FCSTD DOCUMENT  (FreeCAD 1.0R39319 (Git))
Label: trofast-fix
License: All rights reserved
LicenseURL: https://en.wikipedia.org/wiki/All_rights_reserved
objects: Sketcher::SketchObject×1
note: 2 computed .brp shape members not serialized (recipe doc carries the construction recipe); baked Part::Feature solids carry a one-line shape summary decoded from their .brp

FEATURE [Sketcher::SketchObject] Sketch
  ArcFitTolerance = 1e-06
  FullyConstrained = true
  MakeInternals = false
  sketch-geometry (18):
    g0: LineSegment StartX=207.5 StartY=-7.5 StartZ=0 EndX=207.5 EndY=7.5 EndZ=0
    g1: LineSegment StartX=202.5 StartY=12.5 StartZ=0 EndX=-202.5 EndY=12.5 EndZ=0
    g2: LineSegment StartX=-207.5 StartY=7.5 StartZ=0 EndX=-207.5 EndY=-7.5 EndZ=0
    g3: LineSegment StartX=-202.5 StartY=-12.5 StartZ=0 EndX=202.5 EndY=-12.5 EndZ=0
    g4: GeomPoint [constr] X=0 Y=0 Z=0
    g5: Circle CenterX=-182.5 CenterY=0 CenterZ=0 NormalX=0 NormalY=0 NormalZ=1 AngleXU=0 Radius=2
    g6: Circle CenterX=0 CenterY=0 CenterZ=0 NormalX=0 NormalY=0 NormalZ=1 AngleXU=0 Radius=2
    g7: Circle CenterX=182.5 CenterY=0 CenterZ=0 NormalX=0 NormalY=0 NormalZ=1 AngleXU=0 Radius=2
    g8: LineSegment [constr] StartX=-182.5 StartY=0 StartZ=0 EndX=-207.5 EndY=0 EndZ=0
    g9: LineSegment [constr] StartX=182.5 StartY=0 StartZ=0 EndX=207.5 EndY=0 EndZ=0
    g10: ArcOfCircle CenterX=202.5 CenterY=7.5 CenterZ=0 NormalX=0 NormalY=0 NormalZ=1 AngleXU=0 Radius=5 StartAngle=1.32e-14 EndAngle=1.5708
    g11: GeomPoint [constr] X=207.5 Y=12.5 Z=0
    g12: ArcOfCircle CenterX=202.5 CenterY=-7.5 CenterZ=0 NormalX=0 NormalY=0 NormalZ=1 AngleXU=0 Radius=5 StartAngle=4.71239 EndAngle=6.28319
    g13: GeomPoint [constr] X=207.5 Y=-12.5 Z=0
    g14: ArcOfCircle CenterX=-202.5 CenterY=7.5 CenterZ=0 NormalX=0 NormalY=0 NormalZ=1 AngleXU=0 Radius=5 StartAngle=1.5708 EndAngle=3.14159
    g15: GeomPoint [constr] X=-207.5 Y=12.5 Z=0
    g16: ArcOfCircle CenterX=-202.5 CenterY=-7.5 CenterZ=0 NormalX=0 NormalY=0 NormalZ=1 AngleXU=0 Radius=5 StartAngle=3.14159 EndAngle=4.71239
    g17: GeomPoint [constr] X=-207.5 Y=-12.5 Z=0
  constraints (41):
    c: Vertical(g0)
    c: Vertical(g2)
    c: Horizontal(g1)
    c: Horizontal(g3)
    c: Symmetric(g15,g13,g4)
    c: Coincident(g4,g-1)
    c: DistanceX(g15,g11) = 415
    c: DistanceY(g13,g11) = 25
    c: PointOnObject(g5,g-1)
    c: Coincident(g6,g4)
    c: PointOnObject(g7,g-1)
    c: Equal(g5,g6)
    c: Equal(g7,g6)
    c: Coincident(g8,g5)
    c: Symmetric(g15,g17,g8)
    c: Coincident(g9,g7)
    c: PointOnObject(g9,g-1)
    c: Equal(g8,g9)
    c: Diameter(g6) = 4
    c: DistanceX(g8,g8) = 25
    c: PointOnObject(g9,g0)
    c: PointOnObject(g11,g1)
    c: PointOnObject(g11,g0)
    c: Tangent(g1,g10) = -1.5708
    c: Tangent(g0,g10) = -1.5708
    c: PointOnObject(g13,g3)
    c: PointOnObject(g13,g0)
    c: Tangent(g3,g12) = -1.5708
    c: Tangent(g0,g12) = -1.5708
    c: PointOnObject(g15,g1)
    c: PointOnObject(g15,g2)
    c: Tangent(g1,g14) = -1.5708
    c: Tangent(g2,g14) = -1.5708
    c: PointOnObject(g17,g2)
    c: PointOnObject(g17,g3)
    c: Tangent(g2,g16) = -1.5708
    c: Tangent(g3,g16) = -1.5708
    c: Equal(g14,g16)
    c: Equal(g14,g10)
    c: Equal(g12,g14)
    c: Radius(g14) = 5
